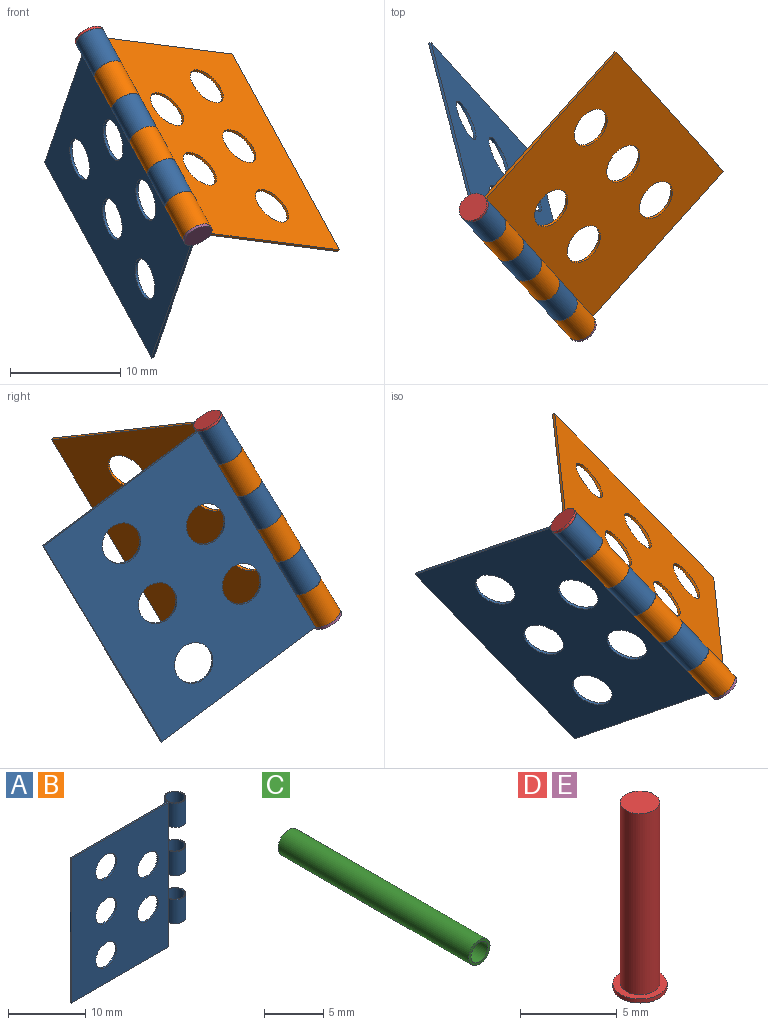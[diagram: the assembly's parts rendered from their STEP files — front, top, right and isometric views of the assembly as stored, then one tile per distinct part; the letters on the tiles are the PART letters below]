
ASSEMBLY  parts=5 mates=4
PART A: 22 faces, bbox 20.6x2.8x22.9 mm
  f0: plane 22.86x0.25mm, normal (1,0,0), area 4.4mm2, adj f1,f2,f8,f10,f11,f12,f13,f14
  f1: plane 22.86x17.78mm, normal (0,1,0), area 349.4mm2, adj f0,f2,f3,f4,f5,f6,f7,f8
  f2: plane 20.57x2.79mm, normal (0,0,1), area 5.6mm2, adj f0,f1,f3,f10,f11,f21
  f3: plane 22.86x0.25mm, normal (-1,0,0), area 5.8mm2, adj f1,f2,f8,f10
  f4: cylinder r=1.91mm len=3.81mm, axis (0,1,0), area 3mm2, adj f1,f10
  f5: cylinder r=1.91mm len=3.81mm, axis (0,1,0), area 3mm2, adj f1,f10
  f6: cylinder r=1.91mm len=3.81mm, axis (0,1,0), area 3mm2, adj f1,f10
  f7: cylinder r=1.91mm len=3.81mm, axis (0,1,0), area 3mm2, adj f1,f10
  f8: plane 17.78x0.25mm, normal (0,0,-1), area 4.5mm2, adj f0,f1,f3,f10
  f9: cylinder r=1.91mm len=3.81mm, axis (0,1,0), area 3mm2, adj f1,f10
  f10: plane 22.86x17.78mm, normal (0,-1,0), area 349.4mm2, adj f0,f2,f3,f4,f5,f6,f7,f8
  f11: cylinder r=1.4mm len=3.81mm, axis (0,0,1), area 33mm2, adj f0,f1,f2,f12
  f12: plane 2.79x2.79mm, normal (0,0,-1), area 1.1mm2, adj f0,f1,f11,f21
  f13: cylinder r=1.4mm len=3.81mm, axis (0,0,1), area 33mm2, adj f0,f1,f14,f15
  f14: plane 2.79x2.79mm, normal (0,0,-1), area 1.1mm2, adj f0,f1,f13,f20
  f15: plane 2.79x2.79mm, normal (0,0,1), area 1.1mm2, adj f0,f1,f13,f20
  f16: cylinder r=1.4mm len=3.81mm, axis (0,0,1), area 33mm2, adj f0,f1,f17,f18
  f17: plane 2.79x2.79mm, normal (0,0,-1), area 1.1mm2, adj f0,f1,f16,f19
  f18: plane 2.79x2.79mm, normal (0,0,1), area 1.1mm2, adj f0,f1,f16,f19
  f19: cylinder r=1.27mm len=3.81mm, axis (0,0,1), area 30.4mm2, adj f17,f18
  f20: cylinder r=1.27mm len=3.81mm, axis (0,0,1), area 30.4mm2, adj f14,f15
  f21: cylinder r=1.27mm len=3.81mm, axis (0,0,1), area 30.4mm2, adj f2,f12
PART B: same geometry as A
PART C: 4 faces, bbox 2.5x22.9x2.5 mm
  f0: cylinder r=1.27mm len=22.86mm, axis (0,1,0), area 182.4mm2, adj f1,f2
  f1: plane 2.54x2.54mm, normal (0,-1,0), area 1.8mm2, adj f0,f3
  f2: plane 2.54x2.54mm, normal (0,1,0), area 1.8mm2, adj f0,f3
  f3: cylinder r=1.02mm len=22.86mm, axis (0,-1,0), area 145.9mm2, adj f1,f2
PART D: 5 faces, bbox 2.8x2.8x11.7 mm
  f0: cylinder r=1.02mm len=11.43mm, axis (0,0,-1), area 73mm2, adj f1,f3
  f1: plane 2.03x2.03mm, normal (0,0,1), area 3.2mm2, adj f0
  f2: cylinder r=1.4mm len=2.79mm, axis (0,0,-1), area 2.2mm2, adj f3,f4
  f3: plane 2.79x2.79mm, normal (0,0,1), area 2.9mm2, adj f0,f2
  f4: plane 2.79x2.79mm, normal (0,0,-1), area 6.1mm2, adj f2
PART E: same geometry as D
PLACE A rot(axis=(-0.12,-0.51,-0.85),78.9deg) t=(-23.88,-8.4,8.31)mm
PLACE B rot(axis=(-0.4,0.86,-0.32),168.6deg) t=(-5.31,-19.53,-4.31)mm
PLACE C rot(axis=(0.81,0.16,0.56),63.1deg) t=(-21.8,-16.43,14.3)mm
PLACE D rot(axis=(-0.27,0.91,-0.3),163.3deg) t=(-21.9,-16.32,14.49)mm
PLACE E rot(axis=(-0.39,0.08,0.92),112.6deg) t=(-12.01,-27.25,-3.64)mm
MATE revolute B.f11 <-> E.f2  axis (0.42,-0.47,-0.78) through (-12.12,-27.13,-3.44)mm
MATE revolute D.f0 <-> C.f3  axis (0.42,-0.47,-0.78) through (-21.8,-16.43,14.3)mm
MATE revolute A.f11 <-> C.f0  axis (-0.42,0.47,0.78) through (-21.8,-16.43,14.3)mm
MATE revolute E.f2 <-> C.f3  axis (-0.42,0.47,0.78) through (-12.12,-27.13,-3.44)mm
